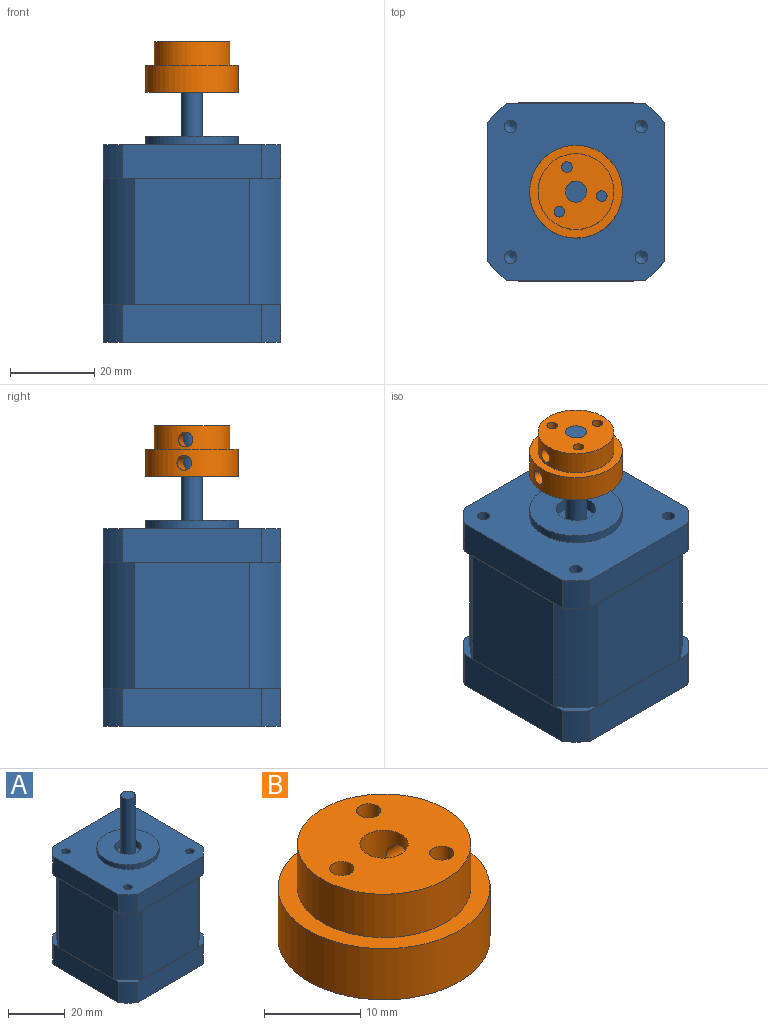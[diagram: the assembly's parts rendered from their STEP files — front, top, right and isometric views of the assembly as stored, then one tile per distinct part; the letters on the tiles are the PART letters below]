
ASSEMBLY  parts=2 mates=1
PART A: 56 faces, bbox 42.2x42.2x71.2 mm
  f0: plane 27.68x0.1mm, normal (0,0,-1), area 2.8mm2, adj f25,f26,f27,f33
  f1: plane 27.68x0.1mm, normal (0,0,-1), area 2.8mm2, adj f20,f21,f27,f35
  f2: plane 27.68x0.1mm, normal (0,0,-1), area 2.8mm2, adj f23,f24,f25,f39
  f3: plane 7.16x7.16mm, normal (0,0,-1), area 12.8mm2, adj f9,f10,f11,f21
  f4: plane 7.16x7.16mm, normal (0,0,-1), area 12.8mm2, adj f11,f12,f13,f23
  f5: plane 7.16x7.16mm, normal (0,0,-1), area 12.8mm2, adj f7,f13,f14,f25
  f6: plane 7.16x7.16mm, normal (0,0,-1), area 12.8mm2, adj f7,f8,f9,f27
  f7: plane 32.98x8mm, normal (1,0,0), area 263.8mm2, adj f5,f6,f8,f14,f15,f18
  f8: cylinder r=26.7mm len=8mm, axis (0,0,1), area 51.2mm2, adj f6,f7,f9,f15
  f9: plane 32.98x8mm, normal (0,1,0), area 263.8mm2, adj f3,f6,f8,f10,f15,f19
  f10: cylinder r=26.7mm len=8mm, axis (0,0,1), area 51.2mm2, adj f3,f9,f11,f15
  f11: plane 32.98x8mm, normal (-1,0,0), area 263.8mm2, adj f3,f4,f10,f12,f15,f17
  f12: cylinder r=26.7mm len=8mm, axis (0,0,1), area 51.2mm2, adj f4,f11,f13,f15
  f13: plane 32.98x8mm, normal (0,-1,0), area 263.8mm2, adj f4,f5,f12,f14,f15,f16
  f14: cylinder r=26.7mm len=8mm, axis (0,0,1), area 51.2mm2, adj f5,f7,f13,f15
  f15: plane 42x42mm, normal (0,0,1), area 1318.2mm2, adj f7,f8,f9,f10,f11,f12,f13,f14
  f16: plane 27.68x0.1mm, normal (0,0,1), area 2.8mm2, adj f13,f23,f24,f25
  f17: plane 27.68x0.1mm, normal (0,0,1), area 2.8mm2, adj f11,f21,f22,f23
  f18: plane 27.68x0.1mm, normal (0,0,1), area 2.8mm2, adj f7,f25,f26,f27
  f19: plane 27.68x0.1mm, normal (0,0,1), area 2.8mm2, adj f9,f20,f21,f27
  f20: plane 29.9x27.37mm, normal (0,1,0), area 818.4mm2, adj f1,f19,f21,f27
  f21: cylinder r=25.15mm len=29.9mm, axis (0,0,-1), area 315.8mm2, adj f1,f3,f17,f19,f20,f22,f28,f32
  f22: plane 29.9x27.37mm, normal (-1,0,0), area 818.4mm2, adj f17,f21,f23,f28
  f23: cylinder r=25.15mm len=29.9mm, axis (0,0,-1), area 315.8mm2, adj f2,f4,f16,f17,f22,f24,f28,f31
  f24: plane 29.9x27.37mm, normal (0,-1,0), area 818.4mm2, adj f2,f16,f23,f25
  f25: cylinder r=25.15mm len=29.9mm, axis (0,0,-1), area 315.8mm2, adj f0,f2,f5,f16,f18,f24,f26,f30
  f26: plane 29.9x27.37mm, normal (1,0,0), area 818.4mm2, adj f0,f18,f25,f27
  f27: cylinder r=25.15mm len=29.9mm, axis (0,0,-1), area 315.8mm2, adj f0,f1,f6,f18,f19,f20,f26,f29
  f28: plane 27.68x0.1mm, normal (0,0,-1), area 2.8mm2, adj f21,f22,f23,f37
  f29: plane 7.16x7.16mm, normal (0,0,1), area 12.8mm2, adj f27,f33,f34,f35
  f30: plane 7.16x7.16mm, normal (0,0,1), area 12.8mm2, adj f25,f33,f39,f40
  f31: plane 7.16x7.16mm, normal (0,0,1), area 12.8mm2, adj f23,f37,f38,f39
  f32: plane 7.16x7.16mm, normal (0,0,1), area 12.8mm2, adj f21,f35,f36,f37
  f33: plane 32.98x8.9mm, normal (1,0,0), area 293.5mm2, adj f0,f29,f30,f34,f40,f41
  f34: cylinder r=26.7mm len=8.9mm, axis (0,0,1), area 56.9mm2, adj f29,f33,f35,f41
  f35: plane 32.98x8.9mm, normal (0,1,0), area 293.5mm2, adj f1,f29,f32,f34,f36,f41
  f36: cylinder r=26.7mm len=8.9mm, axis (0,0,1), area 56.9mm2, adj f32,f35,f37,f41
  f37: plane 32.98x8.9mm, normal (-1,0,0), area 293.5mm2, adj f28,f31,f32,f36,f38,f41
  f38: cylinder r=26.7mm len=8.9mm, axis (0,0,1), area 56.9mm2, adj f31,f37,f39,f41
  f39: plane 32.98x8.9mm, normal (0,-1,0), area 293.5mm2, adj f2,f30,f31,f38,f40,f41
  f40: cylinder r=26.7mm len=8.9mm, axis (0,0,1), area 56.9mm2, adj f30,f33,f39,f41
  f41: plane 42x42mm, normal (0,0,-1), area 1726.6mm2, adj f33,f34,f35,f36,f37,f38,f39,f40
  f42: cylinder r=4.7mm len=9.4mm, axis (0,0,-1), area 88.6mm2, adj f44,f45
  f43: cylinder r=11mm len=22mm, axis (0,0,-1), area 138.2mm2, adj f15,f44
  f44: plane 22x22mm, normal (0,0,1), area 310.7mm2, adj f42,f43
  f45: plane 9.4x9.4mm, normal (0,0,1), area 49.8mm2, adj f42,f47
  f46: plane 5x5mm, normal (0,0,1), area 19.6mm2, adj f47
  f47: cylinder r=2.5mm len=25.4mm, axis (0,0,-1), area 399mm2, adj f45,f46
  f48: cylinder r=1.5mm len=5mm, axis (0,0,1), area 47.1mm2, adj f15,f49
  f49: cone r=0mm half-angle=59deg, axis (0,0,1), area 8.2mm2, adj f48
  f50: cylinder r=1.5mm len=5mm, axis (0,0,1), area 47.1mm2, adj f15,f51
  f51: cone r=0mm half-angle=59deg, axis (0,0,1), area 8.2mm2, adj f50
  f52: cylinder r=1.5mm len=5mm, axis (0,0,1), area 47.1mm2, adj f15,f53
  f53: cone r=0mm half-angle=59deg, axis (0,0,1), area 8.2mm2, adj f52
  f54: cylinder r=1.5mm len=5mm, axis (0,0,1), area 47.1mm2, adj f15,f55
  f55: cone r=0mm half-angle=59deg, axis (0,0,1), area 8.2mm2, adj f54
PART B: 15 faces, bbox 22x22x12 mm
  f0: cylinder r=11mm len=22mm, axis (0,0,-1), area 439.6mm2, adj f3,f4,f13
  f1: cylinder r=2.5mm len=12mm, axis (0,0,-1), area 168.7mm2, adj f4,f5,f9,f10,f11,f12,f13,f14
  f2: cylinder r=9mm len=18mm, axis (0,0,-1), area 301.4mm2, adj f3,f5,f10
  f3: plane 22x22mm, normal (0,0,1), area 125.7mm2, adj f0,f2
  f4: plane 22x22mm, normal (0,0,-1), area 345.8mm2, adj f0,f1,f6,f7,f8
  f5: plane 18x18mm, normal (0,0,1), area 220.1mm2, adj f1,f2,f6,f7,f8
  f6: cylinder r=1.25mm len=12mm, axis (0,0,-1), area 94.2mm2, adj f4,f5
  f7: cylinder r=1.25mm len=12mm, axis (0,0,-1), area 94.2mm2, adj f4,f5
  f8: cylinder r=1.25mm len=12mm, axis (0,0,-1), area 94.2mm2, adj f4,f5
  f9: cone r=0mm half-angle=59deg, axis (1,0,0), area 0.2mm2, adj f1,f10
  f10: cylinder r=1.75mm len=7mm, axis (1,0,0), area 73.8mm2, adj f1,f2,f9,f11
  f11: cone r=0mm half-angle=59deg, axis (1,0,0), area 0.2mm2, adj f1,f10
  f12: cone r=0mm half-angle=59deg, axis (1,0,0), area 0.2mm2, adj f1,f13
  f13: cylinder r=1.75mm len=9mm, axis (1,0,0), area 95.9mm2, adj f0,f1,f12,f14
  f14: cone r=0mm half-angle=59deg, axis (1,0,0), area 0.2mm2, adj f1,f13
PLACE A t=(0,0,-2)mm fixed
PLACE B rot(axis=(0,0,1),170.2deg) t=(0,0,3.4)mm
MATE revolute B.f1 <-> A.f8  axis (0,0,-1) through (0,0,3.4)mm
